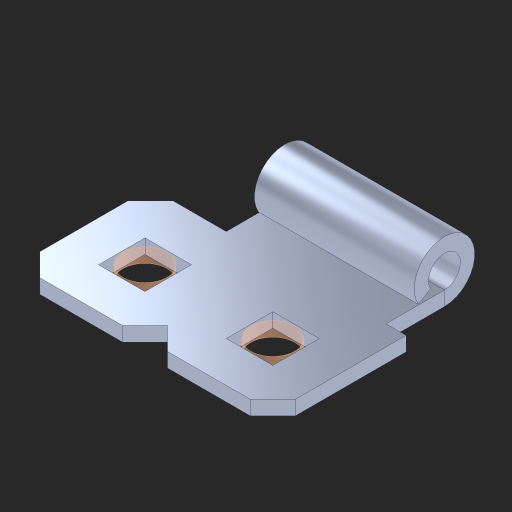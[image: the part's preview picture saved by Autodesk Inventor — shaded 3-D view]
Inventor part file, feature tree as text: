
AUTODESK INVENTOR PART (.ipt)
format: ipt  version: 2023 (Build 270158000, 158)  size: 209,408 bytes
history: native  units: in
note: dims shown in document units (in); Inventor stores cm internally (conversion verified against a paired STEP export)
features: other x4, extrude x3, sketch x2, pattern_linear x1, imported_body x1
ambient origin geometry x8: Origin, YZ Plane, XZ Plane, XY Plane, X Axis, Y Axis, Z Axis, Center Point
bodies: Body1 (feature_tree), Body2 (feature_tree), Body3 (feature_tree)
feature tree (11):
  other  "Cut-Extrude3"
  other  "Bottom"
  pattern_linear  "Rectangular Pattern1"  Spacing1=1.5in  [1 undecoded]
  extrude  "Extrusion1"  Depth=0.5in
  imported_body  "Base1"
  sketch  "Sketch1"  dims[d15=0.046in d16=0.0in]
  other  "Srf1"
  other  "Srf2"
  sketch  "Sketch4"  dims[d19=0.5in d30=1.5in d31=0.0in d32=0.172in]
  extrude  "ExtrusionSrf1"  [1 undecoded]
  extrude  "ExtrusionSrf2"  [1 undecoded]
note: 3 required parameter values undecoded (feature->parameter linkage not recoverable at this tier; creation-order binding heuristic only, values carry confidence <= 0.55)
